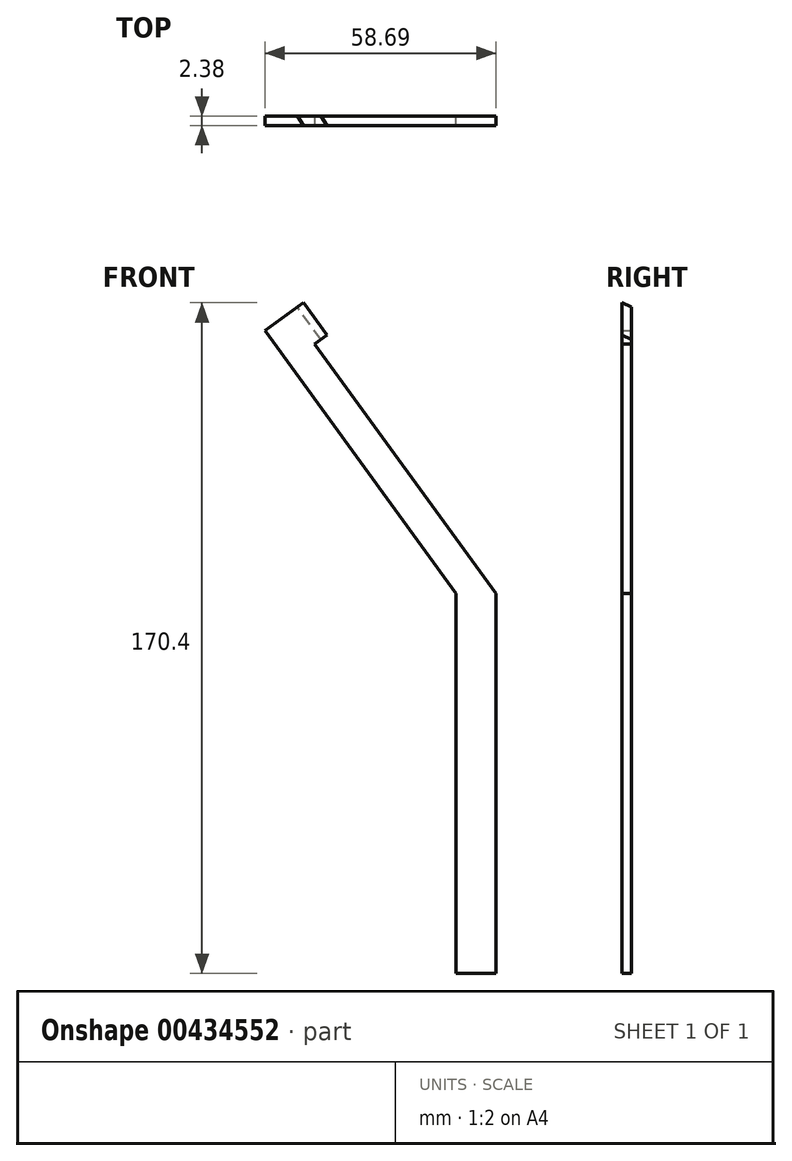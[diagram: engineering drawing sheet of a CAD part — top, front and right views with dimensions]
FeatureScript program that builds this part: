
annotation { "Feature Type Name" : "Feature", "Feature Type Description" : "" }
export const myFeature = defineFeature(function(context is Context, id is Id, definition is map)
    precondition{}
    {
        {
            var Q0;
            Q0=qCreatedBy(makeId("Front.planeOp"),FACE);
            var sketch = newSketch(context, id + "F0", { "sketchPlane" : qUnion([Q0])});
            skLineSegment(sketch, "E0.bottom", {"start": v(0, 0) * mm, "end": v(-10.16, 0) * mm});
            skLineSegment(sketch, "E0.top", {"start": v(0, -96.52) * mm, "end": v(-10.16, -96.52) * mm});
            skLineSegment(sketch, "E0.left", {"start": v(0, 0) * mm, "end": v(0, -96.52) * mm});
            skLineSegment(sketch, "E0.right", {"start": v(-10.16, 0) * mm, "end": v(-10.16, -96.52) * mm});
            skLineSegment(sketch, "E1", {"start": v(-58.69, 66.8) * mm, "end": v(-10.16, 0) * mm});
            skLineSegment(sketch, "E2", {"start": v(0, 0) * mm, "end": v(-48.52, 66.78) * mm});
            skLineSegment(sketch, "E3", {"start": v(-10.16, 0) * mm, "end": v(-10.16, 69.9) * mm});
            skLineSegment(sketch, "E4", {"start": v(-58.69, 66.8) * mm, "end": v(-52.04, 71.62) * mm});
            skLineSegment(sketch, "E5", {"start": v(-48.52, 66.78) * mm, "end": v(-52.04, 71.62) * mm});
            skPoint(sketch, "E6.right.start.orphan", {"position": v(-58.67, 0) * mm});
            skSolve(sketch);
        }
        {
            var Q0;
            Q0 = qSketchRegion(id + "F0", true);
            extrude(context, id + "F1", {"entities" : qUnion([Q0]), "depth" : (2 + (3 / 8)) * mm});
        }
        {
            var Q0;
            Q0=makeQuery(id+"F1.opExtrude","CAP_FACE",FACE,{"disambiguationData":[OSD([sQuery(id+"F0.wireOp",EDGE,"E0.top"),sQuery(id+"F0.wireOp",EDGE,"E0.left"),sQuery(id+"F0.wireOp",EDGE,"E0.right"),sQuery(id+"F0.wireOp",EDGE,"E1"),sQuery(id+"F0.wireOp",EDGE,"E2"),sQuery(id+"F0.wireOp",EDGE,"E4"),sQuery(id+"F0.wireOp",EDGE,"E5")])],"isStart":false});
            var sketch = newSketch(context, id + "F2", { "sketchPlane" : qUnion([Q0])});
            skLineSegment(sketch, "E7", {"start": v(-58.69, 66.8) * mm, "end": v(-38.14, 81.72) * mm});
            skLineSegment(sketch, "E8", {"start": v(-38.14, 81.72) * mm, "end": v(-32.17, 73.5) * mm});
            skLineSegment(sketch, "E9", {"start": v(-32.17, 73.5) * mm, "end": v(-52.72, 58.57) * mm});
            skSolve(sketch);
        }
        {
            var Q0;
            {var subQ3=sQuery(id+"F2.wireOp",EDGE,"E8");Q0=makeQuery(id+"F2.imprint","IMPRINT",FACE,{"disambiguationData":[TD([[makeQuery(id+"F2.imprint","IMPRINT",EDGE,{"derivedFrom":subQ3}),-1.0]])]});}
            extrude(context, id + "F3", {"entities" : qUnion([Q0]), "operationType" : NewBodyOperationType.ADD, "oppositeDirection" : true, "depth" : (2 + (3 / 8)) * mm});
        }
        {
            var Q0;
            Q0=makeQuery(id+"F3.boolean.opBoolean","MERGE",FACE,{"derivedFrom":[makeQuery(id+"F1.opExtrude","SWEPT_FACE",FACE,{"disambiguationData":[OSD([sQuery(id+"F0.wireOp",EDGE,"E4")])]}),makeQuery(id+"F3.opExtrude","SWEPT_FACE",FACE,{"disambiguationData":[OSD([sQuery(id+"F2.wireOp",EDGE,"E7")])]})]});
            var sketch = newSketch(context, id + "F4", { "sketchPlane" : qUnion([Q0])});
            skLineSegment(sketch, "E10.bottom", {"start": v(-8.22, 0) * mm, "end": v(1.94, 0) * mm});
            skLineSegment(sketch, "E10.top", {"start": v(-8.22, -60.33) * mm, "end": v(1.94, -60.33) * mm});
            skLineSegment(sketch, "E10.left", {"start": v(-8.22, 0) * mm, "end": v(-8.22, -60.33) * mm});
            skLineSegment(sketch, "E10.right", {"start": v(1.94, 0) * mm, "end": v(1.94, -60.33) * mm});
            skPoint(sketch, "E11", {"position": v(17.18, -19.05) * mm});
            skPoint(sketch, "E12", {"position": v(17.18, -41.28) * mm});
            skLineSegment(sketch, "E13", {"start": v(1.94, 0) * mm, "end": v(17.18, -19.05) * mm});
            skLineSegment(sketch, "E14", {"start": v(17.18, -41.28) * mm, "end": v(1.94, -60.33) * mm});
            skSolve(sketch);
        }
        {
            var Q0;
            {var subQ0=sQuery(id+"F4.wireOp",EDGE,"E13");Q0=makeQuery(id+"F4.imprint","IMPRINT",FACE,{"disambiguationData":[TD([[makeQuery(id+"F4.imprint","IMPRINT",EDGE,{"derivedFrom":subQ0}),1.0]])]});}
            var Q1;
            {var subQ0=sQuery(id+"F4.wireOp",EDGE,"E14");Q1=makeQuery(id+"F4.imprint","IMPRINT",FACE,{"disambiguationData":[TD([[makeQuery(id+"F4.imprint","IMPRINT",EDGE,{"derivedFrom":subQ0}),1.0]])]});}
            extrude(context, id + "F5", {"entities" : qUnion([Q0, Q1]), "operationType" : NewBodyOperationType.REMOVE, "oppositeDirection" : true, "depth" : 25.4 * mm});
        }
        {
            var Q0;
            Q0=makeQuery(id+"F3.boolean.opBoolean","MERGE",FACE,{"derivedFrom":[makeQuery(id+"F1.opExtrude","SWEPT_FACE",FACE,{"disambiguationData":[OSD([sQuery(id+"F0.wireOp",EDGE,"E4")])]}),makeQuery(id+"F3.opExtrude","SWEPT_FACE",FACE,{"disambiguationData":[OSD([sQuery(id+"F2.wireOp",EDGE,"E7")])]})]});
            var sketch = newSketch(context, id + "F6", { "sketchPlane" : qUnion([Q0])});
            skCircle(sketch, "E15", {"center": v(-4.4, -12.7) * mm, "radius": 3.18 * mm});
            skCircle(sketch, "E16.MirrorC", {"center": v(-4.4, -47.62) * mm, "radius": 3.18 * mm});
            skCircle(sketch, "E17.MirrorC", {"center": v(4.48, -30.16) * mm, "radius": 3.18 * mm});
            skSolve(sketch);
        }
        {
            var Q0;
            Q0 = qSketchRegion(id + "F6", true);
            extrude(context, id + "F7", {"entities" : qUnion([Q0]), "operationType" : NewBodyOperationType.REMOVE, "oppositeDirection" : true, "depth" : 76.2 * mm});
        }
        {
            var Q0;
            Q0=makeQuery(id+"F1.opExtrude","SWEPT_FACE",FACE,{"disambiguationData":[OSD([sQuery(id+"F0.wireOp",EDGE,"E1")])]});
            var sketch = newSketch(context, id + "F8", { "sketchPlane" : qUnion([Q0])});
            skLineSegment(sketch, "E18.left", {"start": v(25.72, 65.03) * mm, "end": v(25.72, 29.47) * mm});
            skLineSegment(sketch, "E18.right", {"start": v(34.6, 65.03) * mm, "end": v(34.6, 29.47) * mm});
            skPoint(sketch, "E19", {"position": v(25.72, 47.25) * mm});
            skPoint(sketch, "E20", {"position": v(34.6, 47.25) * mm});
            skPoint(sketch, "E21", {"position": v(30.16, 69.48) * mm});
            skPoint(sketch, "E22", {"position": v(30.16, 88.53) * mm});
            skPoint(sketch, "E23", {"position": v(30.16, 65.03) * mm});
            skArc(sketch, "E24", {"start": v(34.6, 65.03) * mm, "mid": v(30.16, 69.48) * mm, "end": v(25.72, 65.03) * mm});
            skPoint(sketch, "E25", {"position": v(30.16, 29.47) * mm});
            skPoint(sketch, "E25.positionSnap0", {"position": v(30.16, 25.03) * mm});
            skArc(sketch, "E26", {"start": v(25.72, 29.47) * mm, "mid": v(30.16, 25.03) * mm, "end": v(34.6, 29.47) * mm});
            skPoint(sketch, "E27.orphan", {"position": v(25.72, 25.03) * mm});
            skPoint(sketch, "E28.orphan", {"position": v(34.6, 25.03) * mm});
            skPoint(sketch, "E29.orphan", {"position": v(25.72, 69.48) * mm});
            skPoint(sketch, "E30.orphan", {"position": v(34.6, 69.48) * mm});
            skSolve(sketch);
        }
        {
            var Q0;
            Q0 = qSketchRegion(id + "F8", true);
            extrude(context, id + "F9", {"entities" : qUnion([Q0]), "operationType" : NewBodyOperationType.REMOVE, "oppositeDirection" : true, "depth" : 25.4 * mm});
        }
        {
            var Q0;
            Q0=makeQuery(id+"F1.opExtrude","SWEPT_FACE",FACE,{"disambiguationData":[OSD([sQuery(id+"F0.wireOp",EDGE,"E0.right")])]});
            var sketch = newSketch(context, id + "F10", { "sketchPlane" : qUnion([Q0])});
            skLineSegment(sketch, "E31.left", {"start": v(8.25, -48.26) * mm, "end": v(8.25, -83.82) * mm});
            skLineSegment(sketch, "E31.right", {"start": v(17.14, -48.26) * mm, "end": v(17.14, -83.82) * mm});
            skPoint(sketch, "E32", {"position": v(12.7, -88.27) * mm});
            skPoint(sketch, "E33", {"position": v(12.7, -83.82) * mm});
            skArc(sketch, "E34", {"start": v(8.25, -83.82) * mm, "mid": v(12.7, -88.27) * mm, "end": v(17.15, -83.82) * mm});
            skArc(sketch, "E35.MirrorC", {"start": v(8.25, -48.26) * mm, "mid": v(12.7, -43.82) * mm, "end": v(17.14, -48.26) * mm});
            skPoint(sketch, "E36.end.orphan", {"position": v(8.25, -66.04) * mm});
            skPoint(sketch, "E36.start.orphan", {"position": v(17.14, -66.04) * mm});
            skPoint(sketch, "E37.orphan", {"position": v(8.25, -43.82) * mm});
            skPoint(sketch, "E38.orphan", {"position": v(17.14, -43.82) * mm});
            skPoint(sketch, "E39.orphan", {"position": v(17.15, -88.27) * mm});
            skPoint(sketch, "E40.orphan", {"position": v(8.26, -88.27) * mm});
            skLineSegment(sketch, "E41", {"start": v(30.16, 0) * mm, "end": v(30.16, -96.52) * mm});
            skLineSegment(sketch, "E42.MirrorCS", {"start": v(43.18, -48.26) * mm, "end": v(43.18, -83.82) * mm});
            skArc(sketch, "E43.MirrorCS", {"start": v(52.07, -48.26) * mm, "mid": v(47.63, -43.82) * mm, "end": v(43.18, -48.26) * mm});
            skLineSegment(sketch, "E44.MirrorCS", {"start": v(52.07, -48.26) * mm, "end": v(52.07, -83.82) * mm});
            skArc(sketch, "E45.MirrorCS", {"start": v(52.07, -83.82) * mm, "mid": v(47.62, -88.27) * mm, "end": v(43.18, -83.82) * mm});
            skSolve(sketch);
        }
        {
            var Q0;
            Q0=makeQuery(id+"F10.imprint","IMPRINT",FACE,{"disambiguationData":[TD([[makeQuery(id+"F10.imprint","IMPRINT",EDGE,{"derivedFrom":sQuery(id+"F10.wireOp",EDGE,"E31.left")}),1.0]])]});
            var Q1;
            Q1=makeQuery(id+"F10.imprint","IMPRINT",FACE,{"disambiguationData":[TD([[makeQuery(id+"F10.imprint","IMPRINT",EDGE,{"derivedFrom":sQuery(id+"F10.wireOp",EDGE,"E42.MirrorCS")}),1.0]])]});
            extrude(context, id + "F11", {"entities" : qUnion([Q0, Q1]), "operationType" : NewBodyOperationType.REMOVE, "oppositeDirection" : true, "depth" : 25.4 * mm});
        }
    });
